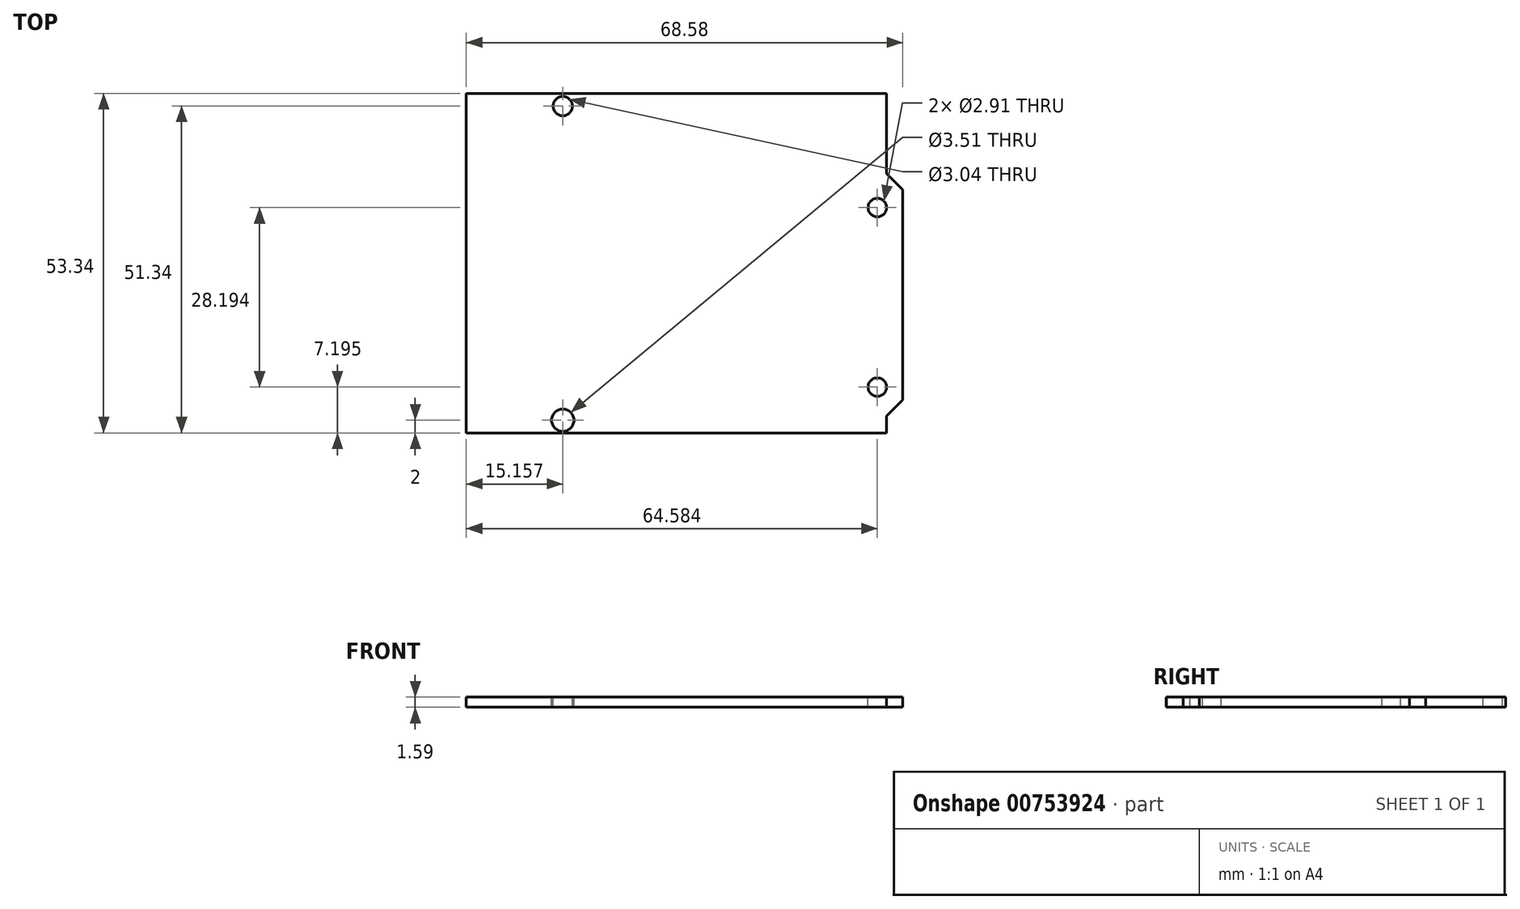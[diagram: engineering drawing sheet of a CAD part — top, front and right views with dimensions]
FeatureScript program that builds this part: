
annotation { "Feature Type Name" : "Feature", "Feature Type Description" : "" }
export const myFeature = defineFeature(function(context is Context, id is Id, definition is map)
    precondition{}
    {
        {
            var Q0;
            Q0=qCreatedBy(makeId("Top.planeOp"),FACE);
            var sketch = newSketch(context, id + "F0", { "sketchPlane" : qUnion([Q0])});
            skLineSegment(sketch, "E0", {"start": v(-33.02, 26.67) * mm, "end": v(-33.02, -26.67) * mm});
            skLineSegment(sketch, "E1", {"start": v(-33.02, -26.67) * mm, "end": v(33.02, -26.67) * mm});
            skLineSegment(sketch, "E2", {"start": v(33.02, -26.67) * mm, "end": v(33.02, 26.67) * mm});
            skLineSegment(sketch, "E3", {"start": v(33.02, 26.67) * mm, "end": v(-33.02, 26.67) * mm});
            skLineSegment(sketch, "E4", {"start": v(0, 26.67) * mm, "end": v(0, 0) * mm, "construction": true});
            skLineSegment(sketch, "E5", {"start": v(0, 0) * mm, "end": v(-33.02, 0) * mm, "construction": true});
            skLineSegment(sketch, "E6", {"start": v(33.02, -24) * mm, "end": v(35.56, -21.46) * mm});
            skLineSegment(sketch, "E7", {"start": v(35.56, -21.46) * mm, "end": v(35.56, 11.56) * mm});
            skLineSegment(sketch, "E8", {"start": v(35.56, 11.56) * mm, "end": v(33.02, 14.1) * mm});
            skSolve(sketch);
        }
        {
            var Q0;
            Q0=qSketchRegion(id+"F0",true);
            extrude(context, id + "F1", {"entities" : qUnion([Q0]), "depth" : 1.59 * mm, "offsetDistance" : 25 * mm});
        }
        {
            var Q0;
            Q0=makeQuery(id+"F1.opExtrude","CAP_FACE",FACE,{"disambiguationData":[OSD([sQuery(id+"F0.wireOp",EDGE,"E0"),sQuery(id+"F0.wireOp",EDGE,"E1"),sQuery(id+"F0.wireOp",EDGE,"E2"),sQuery(id+"F0.wireOp",EDGE,"E3"),sQuery(id+"F0.wireOp",EDGE,"E6"),sQuery(id+"F0.wireOp",EDGE,"E7"),sQuery(id+"F0.wireOp",EDGE,"E8")])],"isStart":false});
            var sketch = newSketch(context, id + "F2", { "sketchPlane" : qUnion([Q0])});
            skCircle(sketch, "E9", {"center": v(-17.86, 24.67) * mm, "radius": 1.52 * mm});
            skCircle(sketch, "E10", {"center": v(-17.86, -24.67) * mm, "radius": 1.76 * mm});
            skCircle(sketch, "E11", {"center": v(31.56, -19.48) * mm, "radius": 1.46 * mm});
            skCircle(sketch, "E12", {"center": v(31.56, 8.72) * mm, "radius": 1.46 * mm});
            skSolve(sketch);
        }
        {
            var Q0;
            Q0=qSketchRegion(id+"F2",true);
            extrude(context, id + "F3", {"entities" : qUnion([Q0]), "operationType" : NewBodyOperationType.REMOVE, "oppositeDirection" : true, "depth" : 25 * mm, "offsetDistance" : 25 * mm});
        }
    });
